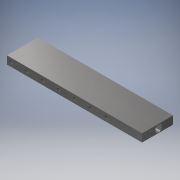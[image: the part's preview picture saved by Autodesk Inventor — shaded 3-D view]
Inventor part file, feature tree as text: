
AUTODESK INVENTOR PART (.ipt)
format: ipt  version: 2018 (Build 220112000, 112)  size: 278,528 bytes
history: native  units: mm
features: hole x8, extrude x1, pattern_linear x1
ambient origin geometry x8: Origin, YZ Plane, XZ Plane, XY Plane, X Axis, Y Axis, Z Axis, Center Point
bodies: Volumenkörper1 (feature_tree)
feature tree (10):
  extrude  "Extrusion1"  Depth=39.0mm
  hole  "Bohrung7"  [1 undecoded]
  hole  "Bohrung8"  [1 undecoded]
  hole  "Bohrung9"  [1 undecoded]
  hole  "Bohrung10"  [1 undecoded]
  pattern_linear  "Rechteckige Anordnung3"  Spacing1=18.8mm  [1 undecoded]
  hole  "Bohrung25"  [1 undecoded]
  hole  "Bohrung26"  [1 undecoded]
  hole  "Bohrung27"  [1 undecoded]
  hole  "Bohrung28"  [1 undecoded]
note: 9 required parameter values undecoded (feature->parameter linkage not recoverable at this tier; creation-order binding heuristic only, values carry confidence <= 0.55)
